# Revit family: Specialty Equipment_Shower Seat_Metlam_ML994CL
name_source: partatom
category: Specialty Equipment
revit_build: Autodesk Revit 2014 (Build: 20130308_1515(x64)
units: mm (PartAtom-declared; Revit-internal decimal feet)

## types (1)
- 960w x 295h x 400d
    Assembly Code = C1030200
    Description = Folding Shower Seat
    Frame Material = z_Metlam_Stainless Steel
    Manufacturer = Metlam
    Manufacturer_Overall Depth = 400 mm  [stored 1.31234 ft]
    Manufacturer_Overall Height = 295 mm  [stored 0.967848 ft]
    Manufacturer_Overall Width = 960 mm  [stored 3.14961 ft]
    Manufacturer_Spec Code = ML994CL
    Manufacturer_URL_Home Page = http://www.metlam.com.au
    Manufacturer_URL__Product Specific = http://metlam.com.au
    Model = ML994CL
    ModifiedIssue_ANZRS = 20151029 $
    Seat Edge Material = z_Metlam_Black
    Seat Material = z_Metlam_White Laminate
    Type Comments = Shower Seats
    URL = http://www.metlam.com.au

note: [stored X ft] marks values corroborated as IEEE doubles in the binary element streams (Revit-internal decimal feet)

## geometry (parser evidence)
native form markers: Sweep x1
no freeform markers — native parametric forms only
